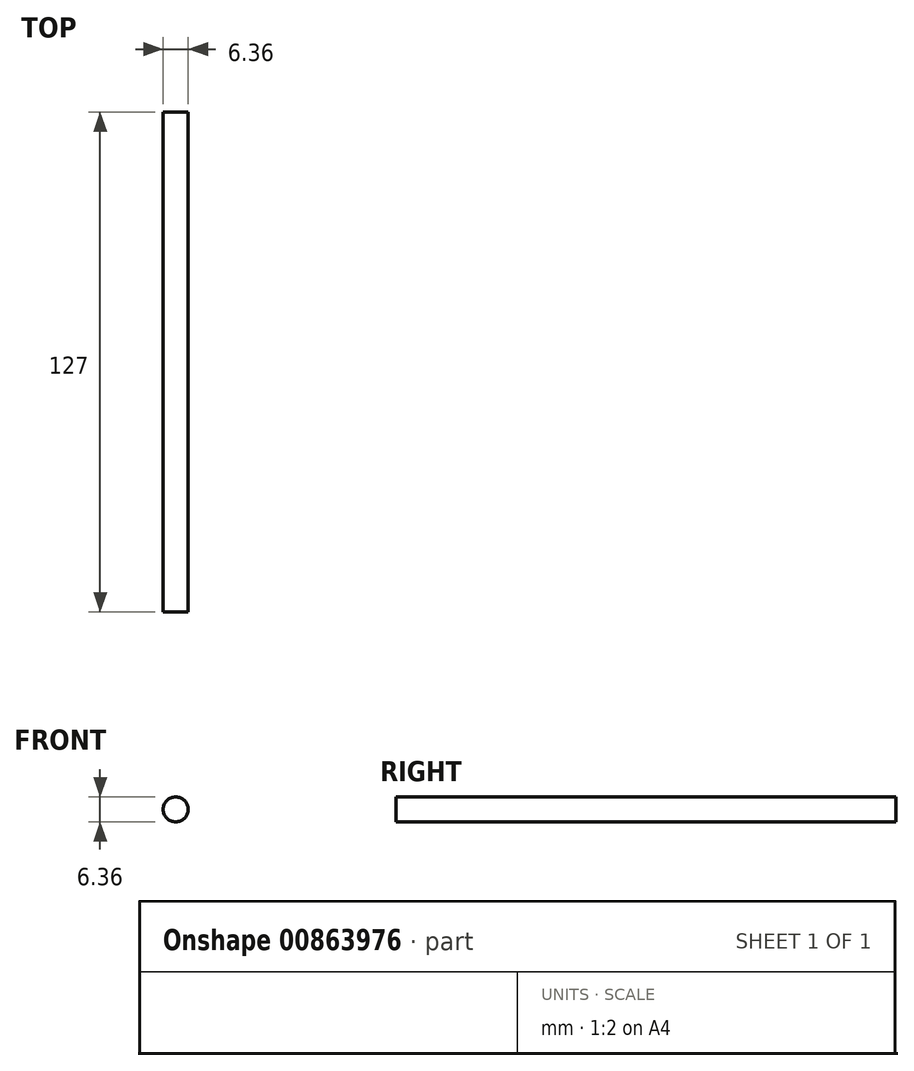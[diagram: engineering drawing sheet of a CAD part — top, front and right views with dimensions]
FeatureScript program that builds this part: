
annotation { "Feature Type Name" : "Feature", "Feature Type Description" : "" }
export const myFeature = defineFeature(function(context is Context, id is Id, definition is map)
    precondition{}
    {
        {
            var Q0;
            Q0=qCreatedBy(makeId("Front.planeOp"),FACE);
            var sketch = newSketch(context, id + "F0", { "sketchPlane" : qUnion([Q0])});
            skCircle(sketch, "E0", {"center": v(0, 0) * mm, "radius": 3.17 * mm});
            skSolve(sketch);
        }
        {
            var Q0;
            Q0 = qSketchRegion(id + "F0", true);
            extrude(context, id + "F1", {"entities" : qUnion([Q0]), "depth" : 127 * mm, "offsetDistance" : 25.4 * mm});
        }
    });
